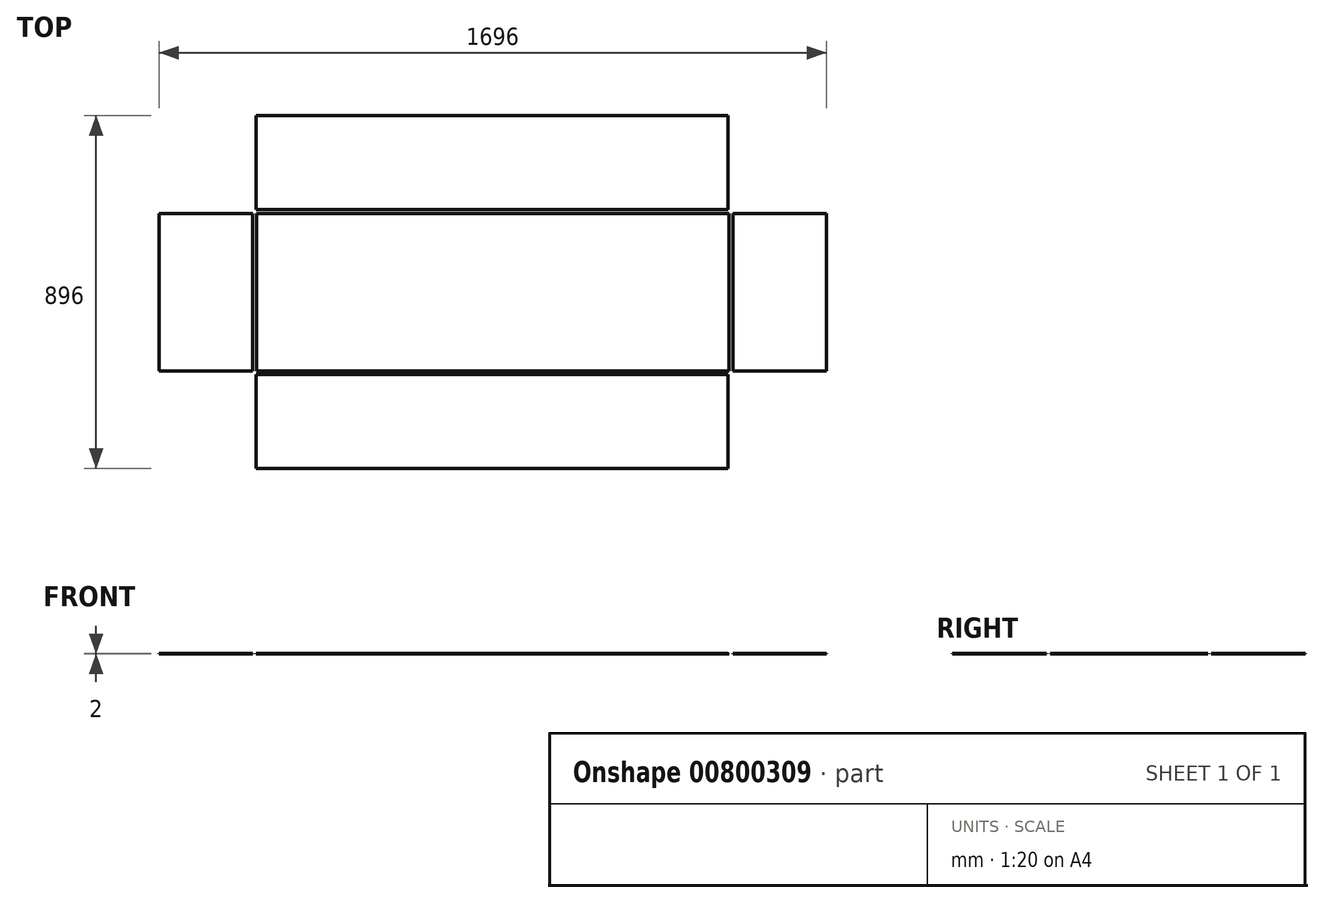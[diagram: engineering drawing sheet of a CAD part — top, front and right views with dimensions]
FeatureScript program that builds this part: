
annotation { "Feature Type Name" : "Feature", "Feature Type Description" : "" }
export const myFeature = defineFeature(function(context is Context, id is Id, definition is map)
    precondition{}
    {
        {
            var Q0;
            Q0=qCreatedBy(makeId("Top.planeOp"),FACE);
            var sketch = newSketch(context, id + "F0", { "sketchPlane" : qUnion([Q0])});
            skLineSegment(sketch, "E0.bottom", {"start": v(600, -200) * mm, "end": v(-600, -200) * mm});
            skLineSegment(sketch, "E0.top", {"start": v(600, 200) * mm, "end": v(-600, 200) * mm});
            skLineSegment(sketch, "E0.left", {"start": v(600, -200) * mm, "end": v(600, 200) * mm});
            skLineSegment(sketch, "E0.right", {"start": v(-600, -200) * mm, "end": v(-600, 200) * mm});
            skPoint(sketch, "E0.middle", {"position": v(0, 0) * mm});
            skSolve(sketch);
        }
        {
            var Q0;
            Q0=makeQuery(id+"F0.imprint","IMPRINT",FACE,{"disambiguationData":[TD([[makeQuery(id+"F0.imprint","IMPRINT",EDGE,{"derivedFrom":sQuery(id+"F0.wireOp",EDGE,"E0.bottom")}),-1.0]])]});
            extrude(context, id + "F1", {"entities" : qUnion([Q0]), "depth" : 1 * mm, "offsetDistance" : 25 * mm});
        }
        {
            var Q0;
            Q0=makeQuery(id+"F1.opExtrude","CAP_FACE",FACE,{"disambiguationData":[OSD([sQuery(id+"F0.wireOp",EDGE,"E0.bottom"),sQuery(id+"F0.wireOp",EDGE,"E0.top"),sQuery(id+"F0.wireOp",EDGE,"E0.left"),sQuery(id+"F0.wireOp",EDGE,"E0.right")])],"isStart":false});
            var sketch = newSketch(context, id + "F2", { "sketchPlane" : qUnion([Q0])});
            skLineSegment(sketch, "E1.bottom", {"start": v(610, 200) * mm, "end": v(848, 200) * mm});
            skLineSegment(sketch, "E1.top", {"start": v(610, -200) * mm, "end": v(848, -200) * mm});
            skLineSegment(sketch, "E1.left", {"start": v(610, 200) * mm, "end": v(610, -200) * mm});
            skLineSegment(sketch, "E1.right", {"start": v(848, 200) * mm, "end": v(848, -200) * mm});
            skLineSegment(sketch, "E2", {"start": v(0, 200) * mm, "end": v(0, -200) * mm, "construction": true});
            skLineSegment(sketch, "E3.MirrorCS", {"start": v(-610, 200) * mm, "end": v(-610, -200) * mm});
            skLineSegment(sketch, "E4.MirrorCS", {"start": v(-610, 200) * mm, "end": v(-848, 200) * mm});
            skLineSegment(sketch, "E5.MirrorCS", {"start": v(-848, 200) * mm, "end": v(-848, -200) * mm});
            skLineSegment(sketch, "E6.MirrorCS", {"start": v(-610, -200) * mm, "end": v(-848, -200) * mm});
            skSolve(sketch);
        }
        {
            var Q0;
            Q0=makeQuery(id+"F2.imprint","IMPRINT",FACE,{"disambiguationData":[TD([[makeQuery(id+"F2.imprint","IMPRINT",EDGE,{"derivedFrom":makeQuery(id+"F1.opExtrude","CAP_EDGE",EDGE,{"disambiguationData":[OSD([sQuery(id+"F0.wireOp",EDGE,"E0.bottom")])],"isStart":false})}),-1.0]])]});
            var sketch = newSketch(context, id + "F3", { "sketchPlane" : qUnion([Q0])});
            skLineSegment(sketch, "E7.bottom", {"start": v(-602.1, -210) * mm, "end": v(597.9, -210) * mm});
            skLineSegment(sketch, "E7.top", {"start": v(-602.1, -448) * mm, "end": v(597.9, -448) * mm});
            skLineSegment(sketch, "E7.left", {"start": v(-602.1, -210) * mm, "end": v(-602.1, -448) * mm});
            skLineSegment(sketch, "E7.right", {"start": v(597.9, -210) * mm, "end": v(597.9, -448) * mm});
            skLineSegment(sketch, "E8.MirrorCS", {"start": v(-602.1, 210) * mm, "end": v(597.9, 210) * mm});
            skLineSegment(sketch, "E9.MirrorCS", {"start": v(-602.1, 210) * mm, "end": v(-602.1, 448) * mm});
            skLineSegment(sketch, "E10.MirrorCS", {"start": v(-602.1, 448) * mm, "end": v(597.9, 448) * mm});
            skLineSegment(sketch, "E11.MirrorCS", {"start": v(597.9, 210) * mm, "end": v(597.9, 448) * mm});
            skSolve(sketch);
        }
        {
            var Q0;
            Q0=makeQuery(id+"F3.imprint","IMPRINT",FACE,{"disambiguationData":[TD([[makeQuery(id+"F3.imprint","IMPRINT",EDGE,{"derivedFrom":sQuery(id+"F3.wireOp",EDGE,"E8.MirrorCS")}),1.0]])]});
            var Q1;
            Q1=makeQuery(id+"F2.imprint","IMPRINT",FACE,{"disambiguationData":[TD([[makeQuery(id+"F2.imprint","IMPRINT",EDGE,{"derivedFrom":sQuery(id+"F2.wireOp",EDGE,"E3.MirrorCS")}),-1.0]])]});
            var Q2;
            Q2=makeQuery(id+"F3.imprint","IMPRINT",FACE,{"disambiguationData":[TD([[makeQuery(id+"F3.imprint","IMPRINT",EDGE,{"derivedFrom":sQuery(id+"F3.wireOp",EDGE,"E7.bottom")}),-1.0]])]});
            var Q3;
            Q3=makeQuery(id+"F2.imprint","IMPRINT",FACE,{"disambiguationData":[TD([[makeQuery(id+"F2.imprint","IMPRINT",EDGE,{"derivedFrom":sQuery(id+"F2.wireOp",EDGE,"E1.bottom")}),-1.0]])]});
            extrude(context, id + "F4", {"entities" : qUnion([Q0, Q1, Q2, Q3]), "depth" : 1 * mm, "offsetDistance" : 25 * mm});
        }
    });
